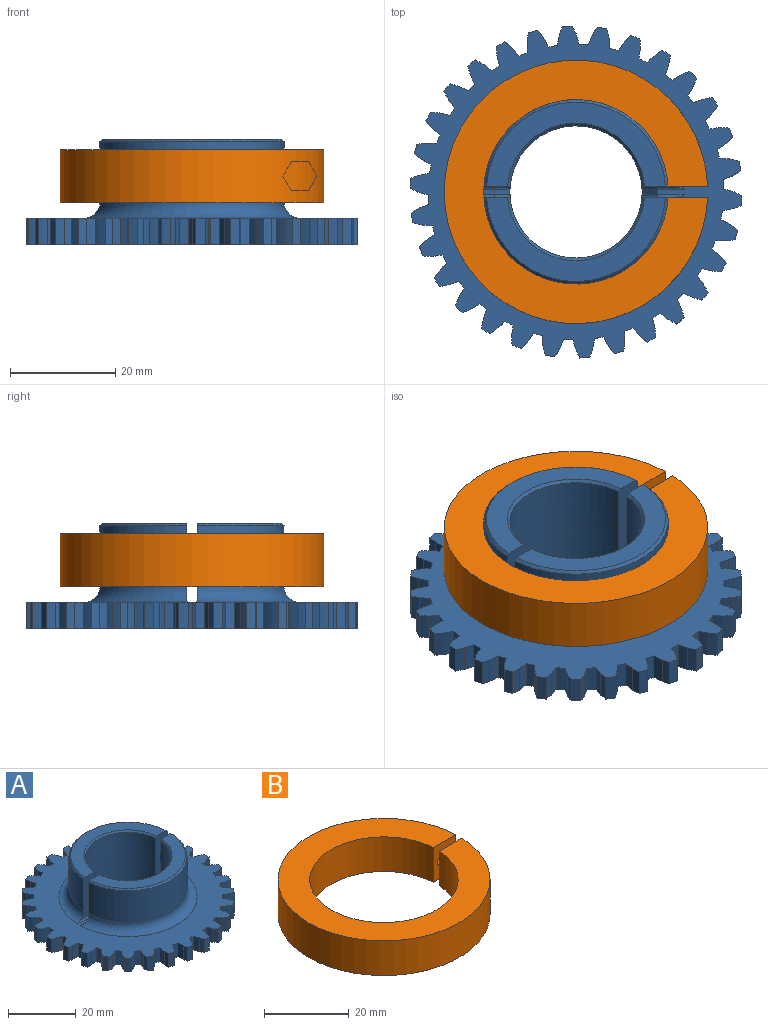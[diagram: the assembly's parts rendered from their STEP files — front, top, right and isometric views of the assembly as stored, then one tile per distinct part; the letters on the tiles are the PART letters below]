
ASSEMBLY  parts=2 mates=1
PART A: 208 faces, bbox 67.7x63x24 mm
  f0: cylinder r=12.55mm len=25.1mm, axis (0,0,-1), area 1428.8mm2, adj f4,f190,f191,f192,f193,f194,f195,f198
  f1: cylinder r=17.5mm len=34.94mm, axis (0,0,-1), area 609.2mm2, adj f3,f192,f194,f197
  f2: plane 33.94x16mm, normal (0,0,1), area 178.5mm2, adj f3,f4,f192,f194
  f3: cone r=17mm half-angle=45deg, axis (0,0,-1), area 36.9mm2, adj f1,f2,f192,f194
  f4: cone r=12.55mm half-angle=45deg, axis (0,0,1), area 27mm2, adj f0,f2,f192,f194
  f5: cylinder r=28mm len=5mm, axis (0,0,-1), area 8.7mm2, adj f9,f16,f181,f188
  f6: cylinder r=15.65mm len=5mm, axis (0,0,-1), area 8.3mm2, adj f7,f10,f181,f188
  f7: cylinder r=31.5mm len=5mm, axis (0,0,-1), area 9.1mm2, adj f6,f8,f181,f188
  f8: cylinder r=15.65mm len=5mm, axis (0,0,-1), area 8.3mm2, adj f7,f9,f181,f188
  f9: cylinder r=17.87mm len=5mm, axis (0,0,-1), area 10.5mm2, adj f5,f8,f181,f188
  f10: cylinder r=17.87mm len=5mm, axis (0,0,-1), area 10.5mm2, adj f6,f181,f182,f188
  f11: cylinder r=28mm len=5mm, axis (0,0,-1), area 8.7mm2, adj f15,f22,f181,f188
  f12: cylinder r=15.65mm len=5mm, axis (0,0,-1), area 8.3mm2, adj f13,f16,f181,f188
  f13: cylinder r=31.5mm len=5mm, axis (0,0,-1), area 9.1mm2, adj f12,f14,f181,f188
  f14: cylinder r=15.65mm len=5mm, axis (0,0,-1), area 8.3mm2, adj f13,f15,f181,f188
  f15: cylinder r=17.87mm len=5mm, axis (0,0,-1), area 10.5mm2, adj f11,f14,f181,f188
  f16: cylinder r=17.87mm len=5mm, axis (0,0,-1), area 10.5mm2, adj f5,f12,f181,f188
  f17: cylinder r=28mm len=5mm, axis (0,0,-1), area 8.7mm2, adj f21,f28,f181,f188
  f18: cylinder r=15.65mm len=5mm, axis (0,0,-1), area 8.3mm2, adj f19,f22,f181,f188
  f19: cylinder r=31.5mm len=5mm, axis (0,0,-1), area 9.1mm2, adj f18,f20,f181,f188
  f20: cylinder r=15.65mm len=5mm, axis (0,0,-1), area 8.3mm2, adj f19,f21,f181,f188
  f21: cylinder r=17.87mm len=5mm, axis (0,0,-1), area 10.5mm2, adj f17,f20,f181,f188
  f22: cylinder r=17.87mm len=5mm, axis (0,0,-1), area 10.5mm2, adj f11,f18,f181,f188
  f23: cylinder r=28mm len=5mm, axis (0,0,-1), area 8.7mm2, adj f27,f34,f181,f188
  f24: cylinder r=15.65mm len=5mm, axis (0,0,-1), area 8.3mm2, adj f25,f28,f181,f188
  f25: cylinder r=31.5mm len=5mm, axis (0,0,-1), area 9.1mm2, adj f24,f26,f181,f188
  f26: cylinder r=15.65mm len=5mm, axis (0,0,-1), area 8.3mm2, adj f25,f27,f181,f188
  f27: cylinder r=17.87mm len=5mm, axis (0,0,-1), area 10.5mm2, adj f23,f26,f181,f188
  f28: cylinder r=17.87mm len=5mm, axis (0,0,-1), area 10.5mm2, adj f17,f24,f181,f188
  f29: cylinder r=28mm len=5mm, axis (0,0,-1), area 8.7mm2, adj f33,f40,f181,f188
  f30: cylinder r=15.65mm len=5mm, axis (0,0,-1), area 8.3mm2, adj f31,f34,f181,f188
  f31: cylinder r=31.5mm len=5mm, axis (0,0,-1), area 9.1mm2, adj f30,f32,f181,f188
  f32: cylinder r=15.65mm len=5mm, axis (0,0,-1), area 8.3mm2, adj f31,f33,f181,f188
  f33: cylinder r=17.87mm len=5mm, axis (0,0,-1), area 10.5mm2, adj f29,f32,f181,f188
  f34: cylinder r=17.87mm len=5mm, axis (0,0,-1), area 10.5mm2, adj f23,f30,f181,f188
  f35: cylinder r=28mm len=5mm, axis (0,0,-1), area 8.7mm2, adj f39,f46,f181,f188
  f36: cylinder r=15.65mm len=5mm, axis (0,0,-1), area 8.3mm2, adj f37,f40,f181,f188
  f37: cylinder r=31.5mm len=5mm, axis (0,0,-1), area 9.1mm2, adj f36,f38,f181,f188
  f38: cylinder r=15.65mm len=5mm, axis (0,0,-1), area 8.3mm2, adj f37,f39,f181,f188
  f39: cylinder r=17.87mm len=5mm, axis (0,0,-1), area 10.5mm2, adj f35,f38,f181,f188
  f40: cylinder r=17.87mm len=5mm, axis (0,0,-1), area 10.5mm2, adj f29,f36,f181,f188
  f41: cylinder r=28mm len=5mm, axis (0,0,-1), area 8.7mm2, adj f45,f52,f181,f188
  f42: cylinder r=15.65mm len=5mm, axis (0,0,-1), area 8.3mm2, adj f43,f46,f181,f188
  f43: cylinder r=31.5mm len=5mm, axis (0,0,-1), area 9.1mm2, adj f42,f44,f181,f188
  f44: cylinder r=15.65mm len=5mm, axis (0,0,-1), area 8.3mm2, adj f43,f45,f181,f188
  f45: cylinder r=17.87mm len=5mm, axis (0,0,-1), area 10.5mm2, adj f41,f44,f181,f188
  f46: cylinder r=17.87mm len=5mm, axis (0,0,-1), area 10.5mm2, adj f35,f42,f181,f188
  f47: cylinder r=28mm len=5mm, axis (0,0,-1), area 8.7mm2, adj f51,f58,f181,f188
  f48: cylinder r=15.65mm len=5mm, axis (0,0,-1), area 8.3mm2, adj f49,f52,f181,f188
  f49: cylinder r=31.5mm len=5mm, axis (0,0,-1), area 9.1mm2, adj f48,f50,f181,f188
  f50: cylinder r=15.65mm len=5mm, axis (0,0,-1), area 8.3mm2, adj f49,f51,f181,f188
  f51: cylinder r=17.87mm len=5mm, axis (0,0,-1), area 10.5mm2, adj f47,f50,f181,f188
  f52: cylinder r=17.87mm len=5mm, axis (0,0,-1), area 10.5mm2, adj f41,f48,f181,f188
  f53: cylinder r=28mm len=5mm, axis (0,0,-1), area 8.7mm2, adj f57,f64,f181,f188
  f54: cylinder r=15.65mm len=5mm, axis (0,0,-1), area 8.3mm2, adj f55,f58,f181,f188
  f55: cylinder r=31.5mm len=5mm, axis (0,0,-1), area 9.1mm2, adj f54,f56,f181,f188
  f56: cylinder r=15.65mm len=5mm, axis (0,0,-1), area 8.3mm2, adj f55,f57,f181,f188
  f57: cylinder r=17.87mm len=5mm, axis (0,0,-1), area 10.5mm2, adj f53,f56,f181,f188
  f58: cylinder r=17.87mm len=5mm, axis (0,0,-1), area 10.5mm2, adj f47,f54,f181,f188
  f59: cylinder r=28mm len=5mm, axis (0,0,-1), area 8.7mm2, adj f63,f70,f181,f188
  f60: cylinder r=15.65mm len=5mm, axis (0,0,-1), area 8.3mm2, adj f61,f64,f181,f188
  f61: cylinder r=31.5mm len=5mm, axis (0,0,-1), area 9.1mm2, adj f60,f62,f181,f188
  f62: cylinder r=15.65mm len=5mm, axis (0,0,-1), area 8.3mm2, adj f61,f63,f181,f188
  f63: cylinder r=17.87mm len=5mm, axis (0,0,-1), area 10.5mm2, adj f59,f62,f181,f188
  f64: cylinder r=17.87mm len=5mm, axis (0,0,-1), area 10.5mm2, adj f53,f60,f181,f188
  f65: cylinder r=28mm len=5mm, axis (0,0,-1), area 8.7mm2, adj f69,f76,f181,f188
  f66: cylinder r=15.65mm len=5mm, axis (0,0,-1), area 8.3mm2, adj f67,f70,f181,f188
  f67: cylinder r=31.5mm len=5mm, axis (0,0,-1), area 9.1mm2, adj f66,f68,f181,f188
  f68: cylinder r=15.65mm len=5mm, axis (0,0,-1), area 8.3mm2, adj f67,f69,f181,f188
  f69: cylinder r=17.87mm len=5mm, axis (0,0,-1), area 10.5mm2, adj f65,f68,f181,f188
  f70: cylinder r=17.87mm len=5mm, axis (0,0,-1), area 10.5mm2, adj f59,f66,f181,f188
  f71: cylinder r=28mm len=5mm, axis (0,0,-1), area 8.7mm2, adj f75,f82,f181,f188
  f72: cylinder r=15.65mm len=5mm, axis (0,0,-1), area 8.3mm2, adj f73,f76,f181,f188
  f73: cylinder r=31.5mm len=5mm, axis (0,0,-1), area 9.1mm2, adj f72,f74,f181,f188
  f74: cylinder r=15.65mm len=5mm, axis (0,0,-1), area 8.3mm2, adj f73,f75,f181,f188
  f75: cylinder r=17.87mm len=5mm, axis (0,0,-1), area 10.5mm2, adj f71,f74,f181,f188
  f76: cylinder r=17.87mm len=5mm, axis (0,0,-1), area 10.5mm2, adj f65,f72,f181,f188
  f77: cylinder r=28mm len=5mm, axis (0,0,-1), area 8.7mm2, adj f81,f88,f181,f188
  f78: cylinder r=15.65mm len=5mm, axis (0,0,-1), area 8.3mm2, adj f79,f82,f181,f188
  f79: cylinder r=31.5mm len=5mm, axis (0,0,-1), area 9.1mm2, adj f78,f80,f181,f188
  f80: cylinder r=15.65mm len=5mm, axis (0,0,-1), area 8.3mm2, adj f79,f81,f181,f188
  f81: cylinder r=17.87mm len=5mm, axis (0,0,-1), area 10.5mm2, adj f77,f80,f181,f188
  f82: cylinder r=17.87mm len=5mm, axis (0,0,-1), area 10.5mm2, adj f71,f78,f181,f188
  f83: cylinder r=28mm len=5mm, axis (0,0,-1), area 8.7mm2, adj f87,f94,f181,f188
  f84: cylinder r=15.65mm len=5mm, axis (0,0,-1), area 8.3mm2, adj f85,f88,f181,f188
  f85: cylinder r=31.5mm len=5mm, axis (0,0,-1), area 9.1mm2, adj f84,f86,f181,f188
  f86: cylinder r=15.65mm len=5mm, axis (0,0,-1), area 8.3mm2, adj f85,f87,f181,f188
  f87: cylinder r=17.87mm len=5mm, axis (0,0,-1), area 10.5mm2, adj f83,f86,f181,f188
  f88: cylinder r=17.87mm len=5mm, axis (0,0,-1), area 10.5mm2, adj f77,f84,f181,f188
  f89: cylinder r=28mm len=5mm, axis (0,0,-1), area 8.7mm2, adj f93,f100,f181,f188
  f90: cylinder r=15.65mm len=5mm, axis (0,0,-1), area 8.3mm2, adj f91,f94,f181,f188
  f91: cylinder r=31.5mm len=5mm, axis (0,0,-1), area 9.1mm2, adj f90,f92,f181,f188
  f92: cylinder r=15.65mm len=5mm, axis (0,0,-1), area 8.3mm2, adj f91,f93,f181,f188
  f93: cylinder r=17.87mm len=5mm, axis (0,0,-1), area 10.5mm2, adj f89,f92,f181,f188
  f94: cylinder r=17.87mm len=5mm, axis (0,0,-1), area 10.5mm2, adj f83,f90,f181,f188
  f95: cylinder r=28mm len=5mm, axis (0,0,-1), area 8.7mm2, adj f99,f106,f181,f188
  f96: cylinder r=15.65mm len=5mm, axis (0,0,-1), area 8.3mm2, adj f97,f100,f181,f188
  f97: cylinder r=31.5mm len=5mm, axis (0,0,-1), area 9.1mm2, adj f96,f98,f181,f188
  f98: cylinder r=15.65mm len=5mm, axis (0,0,-1), area 8.3mm2, adj f97,f99,f181,f188
  f99: cylinder r=17.87mm len=5mm, axis (0,0,-1), area 10.5mm2, adj f95,f98,f181,f188
  f100: cylinder r=17.87mm len=5mm, axis (0,0,-1), area 10.5mm2, adj f89,f96,f181,f188
  f101: cylinder r=28mm len=5mm, axis (0,0,-1), area 8.7mm2, adj f105,f112,f181,f188
  f102: cylinder r=15.65mm len=5mm, axis (0,0,-1), area 8.3mm2, adj f103,f106,f181,f188
  f103: cylinder r=31.5mm len=5mm, axis (0,0,-1), area 9.1mm2, adj f102,f104,f181,f188
  f104: cylinder r=15.65mm len=5mm, axis (0,0,-1), area 8.3mm2, adj f103,f105,f181,f188
  f105: cylinder r=17.87mm len=5mm, axis (0,0,-1), area 10.5mm2, adj f101,f104,f181,f188
  f106: cylinder r=17.87mm len=5mm, axis (0,0,-1), area 10.5mm2, adj f95,f102,f181,f188
  f107: cylinder r=28mm len=5mm, axis (0,0,-1), area 8.7mm2, adj f111,f118,f181,f188
  f108: cylinder r=15.65mm len=5mm, axis (0,0,-1), area 8.3mm2, adj f109,f112,f181,f188
  f109: cylinder r=31.5mm len=5mm, axis (0,0,-1), area 9.1mm2, adj f108,f110,f181,f188
  f110: cylinder r=15.65mm len=5mm, axis (0,0,-1), area 8.3mm2, adj f109,f111,f181,f188
  f111: cylinder r=17.87mm len=5mm, axis (0,0,-1), area 10.5mm2, adj f107,f110,f181,f188
  f112: cylinder r=17.87mm len=5mm, axis (0,0,-1), area 10.5mm2, adj f101,f108,f181,f188
  f113: cylinder r=28mm len=5mm, axis (0,0,-1), area 8.7mm2, adj f117,f124,f181,f188
  f114: cylinder r=15.65mm len=5mm, axis (0,0,-1), area 8.3mm2, adj f115,f118,f181,f188
  f115: cylinder r=31.5mm len=5mm, axis (0,0,-1), area 9.1mm2, adj f114,f116,f181,f188
  f116: cylinder r=15.65mm len=5mm, axis (0,0,-1), area 8.3mm2, adj f115,f117,f181,f188
  f117: cylinder r=17.87mm len=5mm, axis (0,0,-1), area 10.5mm2, adj f113,f116,f181,f188
  f118: cylinder r=17.87mm len=5mm, axis (0,0,-1), area 10.5mm2, adj f107,f114,f181,f188
  f119: cylinder r=28mm len=5mm, axis (0,0,-1), area 8.7mm2, adj f123,f130,f181,f188
  f120: cylinder r=15.65mm len=5mm, axis (0,0,-1), area 8.3mm2, adj f121,f124,f181,f188
  f121: cylinder r=31.5mm len=5mm, axis (0,0,-1), area 9.1mm2, adj f120,f122,f181,f188
  f122: cylinder r=15.65mm len=5mm, axis (0,0,-1), area 8.3mm2, adj f121,f123,f181,f188
  f123: cylinder r=17.87mm len=5mm, axis (0,0,-1), area 10.5mm2, adj f119,f122,f181,f188
  f124: cylinder r=17.87mm len=5mm, axis (0,0,-1), area 10.5mm2, adj f113,f120,f181,f188
  f125: cylinder r=28mm len=5mm, axis (0,0,-1), area 8.7mm2, adj f129,f136,f181,f188
  f126: cylinder r=15.65mm len=5mm, axis (0,0,-1), area 8.3mm2, adj f127,f130,f181,f188
  f127: cylinder r=31.5mm len=5mm, axis (0,0,-1), area 9.1mm2, adj f126,f128,f181,f188
  f128: cylinder r=15.65mm len=5mm, axis (0,0,-1), area 8.3mm2, adj f127,f129,f181,f188
  f129: cylinder r=17.87mm len=5mm, axis (0,0,-1), area 10.5mm2, adj f125,f128,f181,f188
  f130: cylinder r=17.87mm len=5mm, axis (0,0,-1), area 10.5mm2, adj f119,f126,f181,f188
  f131: cylinder r=28mm len=5mm, axis (0,0,-1), area 8.7mm2, adj f135,f142,f181,f188
  f132: cylinder r=15.65mm len=5mm, axis (0,0,-1), area 8.3mm2, adj f133,f136,f181,f188
  f133: cylinder r=31.5mm len=5mm, axis (0,0,-1), area 9.1mm2, adj f132,f134,f181,f188
  f134: cylinder r=15.65mm len=5mm, axis (0,0,-1), area 8.3mm2, adj f133,f135,f181,f188
  f135: cylinder r=17.87mm len=5mm, axis (0,0,-1), area 10.5mm2, adj f131,f134,f181,f188
  f136: cylinder r=17.87mm len=5mm, axis (0,0,-1), area 10.5mm2, adj f125,f132,f181,f188
  f137: cylinder r=28mm len=5mm, axis (0,0,-1), area 8.7mm2, adj f141,f148,f181,f188
  f138: cylinder r=15.65mm len=5mm, axis (0,0,-1), area 8.3mm2, adj f139,f142,f181,f188
  f139: cylinder r=31.5mm len=5mm, axis (0,0,-1), area 9.1mm2, adj f138,f140,f181,f188
  f140: cylinder r=15.65mm len=5mm, axis (0,0,-1), area 8.3mm2, adj f139,f141,f181,f188
  f141: cylinder r=17.87mm len=5mm, axis (0,0,-1), area 10.5mm2, adj f137,f140,f181,f188
  f142: cylinder r=17.87mm len=5mm, axis (0,0,-1), area 10.5mm2, adj f131,f138,f181,f188
  f143: cylinder r=28mm len=5mm, axis (0,0,-1), area 8.7mm2, adj f147,f154,f181,f188
  f144: cylinder r=15.65mm len=5mm, axis (0,0,-1), area 8.3mm2, adj f145,f148,f181,f188
  f145: cylinder r=31.5mm len=5mm, axis (0,0,-1), area 9.1mm2, adj f144,f146,f181,f188
  f146: cylinder r=15.65mm len=5mm, axis (0,0,-1), area 8.3mm2, adj f145,f147,f181,f188
  f147: cylinder r=17.87mm len=5mm, axis (0,0,-1), area 10.5mm2, adj f143,f146,f181,f188
  f148: cylinder r=17.87mm len=5mm, axis (0,0,-1), area 10.5mm2, adj f137,f144,f181,f188
  f149: cylinder r=28mm len=5mm, axis (0,0,-1), area 8.7mm2, adj f153,f160,f181,f188
  f150: cylinder r=15.65mm len=5mm, axis (0,0,-1), area 8.3mm2, adj f151,f154,f181,f188
  f151: cylinder r=31.5mm len=5mm, axis (0,0,-1), area 9.1mm2, adj f150,f152,f181,f188
  f152: cylinder r=15.65mm len=5mm, axis (0,0,-1), area 8.3mm2, adj f151,f153,f181,f188
  f153: cylinder r=17.87mm len=5mm, axis (0,0,-1), area 10.5mm2, adj f149,f152,f181,f188
  f154: cylinder r=17.87mm len=5mm, axis (0,0,-1), area 10.5mm2, adj f143,f150,f181,f188
  f155: cylinder r=28mm len=5mm, axis (0,0,-1), area 8.7mm2, adj f159,f166,f181,f188
  f156: cylinder r=15.65mm len=5mm, axis (0,0,-1), area 8.3mm2, adj f157,f160,f181,f188
  f157: cylinder r=31.5mm len=5mm, axis (0,0,-1), area 9.1mm2, adj f156,f158,f181,f188
  f158: cylinder r=15.65mm len=5mm, axis (0,0,-1), area 8.3mm2, adj f157,f159,f181,f188
  f159: cylinder r=17.87mm len=5mm, axis (0,0,-1), area 10.5mm2, adj f155,f158,f181,f188
  f160: cylinder r=17.87mm len=5mm, axis (0,0,-1), area 10.5mm2, adj f149,f156,f181,f188
  f161: cylinder r=28mm len=5mm, axis (0,0,-1), area 8.7mm2, adj f165,f172,f181,f188
  f162: cylinder r=15.65mm len=5mm, axis (0,0,-1), area 8.3mm2, adj f163,f166,f181,f188
  f163: cylinder r=31.5mm len=5mm, axis (0,0,-1), area 9.1mm2, adj f162,f164,f181,f188
  f164: cylinder r=15.65mm len=5mm, axis (0,0,-1), area 8.3mm2, adj f163,f165,f181,f188
  f165: cylinder r=17.87mm len=5mm, axis (0,0,-1), area 10.5mm2, adj f161,f164,f181,f188
  f166: cylinder r=17.87mm len=5mm, axis (0,0,-1), area 10.5mm2, adj f155,f162,f181,f188
  f167: cylinder r=28mm len=5mm, axis (0,0,-1), area 8.7mm2, adj f171,f178,f181,f188
  f168: cylinder r=15.65mm len=5mm, axis (0,0,-1), area 8.3mm2, adj f169,f172,f181,f188
  f169: cylinder r=31.5mm len=5mm, axis (0,0,-1), area 9.1mm2, adj f168,f170,f181,f188
  f170: cylinder r=15.65mm len=5mm, axis (0,0,-1), area 8.3mm2, adj f169,f171,f181,f188
  f171: cylinder r=17.87mm len=5mm, axis (0,0,-1), area 10.5mm2, adj f167,f170,f181,f188
  f172: cylinder r=17.87mm len=5mm, axis (0,0,-1), area 10.5mm2, adj f161,f168,f181,f188
  f173: cylinder r=28mm len=5mm, axis (0,0,-1), area 8.7mm2, adj f177,f181,f183,f188
  f174: cylinder r=15.65mm len=5mm, axis (0,0,-1), area 8.3mm2, adj f175,f178,f181,f188
  f175: cylinder r=31.5mm len=5mm, axis (0,0,-1), area 9.1mm2, adj f174,f176,f181,f188
  f176: cylinder r=15.65mm len=5mm, axis (0,0,-1), area 8.3mm2, adj f175,f177,f181,f188
  f177: cylinder r=17.87mm len=5mm, axis (0,0,-1), area 10.5mm2, adj f173,f176,f181,f188
  f178: cylinder r=17.87mm len=5mm, axis (0,0,-1), area 10.5mm2, adj f167,f174,f181,f188
  f179: cylinder r=17.5mm len=34.94mm, axis (0,0,-1), area 609.2mm2, adj f189,f193,f195,f196
  f180: plane 33.94x16mm, normal (0,0,1), area 178.5mm2, adj f189,f191,f193,f195
  f181: plane 62.98x62.98mm, normal (0,0,-1), area 2262mm2, adj f5,f6,f7,f8,f9,f10,f11,f12
  f182: cylinder r=28mm len=5mm, axis (0,0,-1), area 8.7mm2, adj f10,f181,f187,f188
  f183: cylinder r=17.87mm len=5mm, axis (0,0,-1), area 10.5mm2, adj f173,f181,f184,f188
  f184: cylinder r=15.65mm len=5mm, axis (0,0,-1), area 8.3mm2, adj f181,f183,f185,f188
  f185: cylinder r=31.5mm len=5mm, axis (0,0,-1), area 9.1mm2, adj f181,f184,f186,f188
  f186: cylinder r=15.65mm len=5mm, axis (0,0,-1), area 8.3mm2, adj f181,f185,f187,f188
  f187: cylinder r=17.87mm len=5mm, axis (0,0,-1), area 10.5mm2, adj f181,f182,f186,f188
  f188: plane 62.98x62.98mm, normal (0,0,1), area 1486.6mm2, adj f5,f6,f7,f8,f9,f10,f11,f12
  f189: cone r=17mm half-angle=45deg, axis (0,0,-1), area 36.9mm2, adj f179,f180,f193,f195
  f190: cone r=13.05mm half-angle=45deg, axis (0,0,-1), area 56.9mm2, adj f0,f181
  f191: cone r=12.55mm half-angle=45deg, axis (0,0,1), area 27mm2, adj f0,f180,f193,f195
  f192: plane 17.35x6.34mm, normal (0,-1,0), area 76.7mm2, adj f0,f1,f2,f3,f4,f197,f206,f207
  f193: plane 17.35x6.34mm, normal (0,1,0), area 76.7mm2, adj f0,f179,f180,f189,f191,f196,f204,f205
  f194: plane 17.35x6.34mm, normal (0,-1,0), area 76.7mm2, adj f0,f1,f2,f3,f4,f197,f200,f201
  f195: plane 17.35x6.34mm, normal (0,1,0), area 76.7mm2, adj f0,f179,f180,f189,f191,f196,f202,f203
  f196: torus R=20.5mm, axis (0,0,1), area 266.7mm2, adj f179,f188,f193,f195,f202,f204
  f197: torus R=20.5mm, axis (0,0,1), area 266.7mm2, adj f1,f188,f192,f194,f200,f206
  f198: cone r=12.55mm half-angle=45deg, axis (0,0,1), area 4.4mm2, adj f0,f188,f204,f205,f206,f207
  f199: cone r=12.55mm half-angle=45deg, axis (0,0,1), area 4.4mm2, adj f0,f188,f200,f201,f202,f203
  f200: cylinder r=0.5mm len=5.16mm, axis (-1,0,0), area 3.2mm2, adj f188,f194,f197,f199,f201
  f201: bspline ~23.95x23.94mm, area 3.2mm2, adj f0,f194,f199,f200
  f202: cylinder r=0.5mm len=5.16mm, axis (1,0,0), area 3.2mm2, adj f188,f195,f196,f199,f203
  f203: bspline ~23.95x23.94mm, area 3.2mm2, adj f0,f195,f199,f202
  f204: cylinder r=0.5mm len=5.16mm, axis (1,0,0), area 3.2mm2, adj f188,f193,f196,f198,f205
  f205: bspline ~23.95x23.94mm, area 3.2mm2, adj f0,f193,f198,f204
  f206: cylinder r=0.5mm len=5.16mm, axis (-1,0,0), area 3.2mm2, adj f188,f192,f197,f198,f207
  f207: bspline ~23.95x23.94mm, area 3.2mm2, adj f0,f192,f198,f206
PART B: 19 faces, bbox 50x50.1x10.1 mm
  f0: cylinder r=25mm len=50mm, axis (0,0,-1), area 1499.6mm2, adj f1,f2,f3,f4,f5
  f1: plane 10x7.51mm, normal (0,-1,0), area 67mm2, adj f0,f2,f4,f6,f7
  f2: plane 50x49.98mm, normal (0,0,-1), area 986.4mm2, adj f0,f1,f3,f7
  f3: plane 10x7.51mm, normal (0,1,0), area 67mm2, adj f0,f2,f4,f7,f8
  f4: plane 50x49.98mm, normal (0,0,1), area 986.4mm2, adj f0,f1,f3,f7
  f5: cylinder r=3mm len=12.88mm, axis (0,-1,0), area 166.3mm2, adj f0,f9
  f6: cylinder r=1.6mm len=3.2mm, axis (0,-1,0), area 30.2mm2, adj f1,f10
  f7: cylinder r=17.5mm len=35mm, axis (0,0,-1), area 1079.5mm2, adj f1,f2,f3,f4
  f8: cylinder r=1.6mm len=4mm, axis (0,-1,0), area 40.2mm2, adj f3,f11
  f9: plane 6x6mm, normal (0,1,0), area 7mm2, adj f5,f10
  f10: cone r=1.6mm half-angle=45deg, axis (0,1,0), area 18.7mm2, adj f6,f9
  f11: plane 6.47x5.6mm, normal (0,-1,0), area 19.1mm2, adj f8,f12,f13,f14,f15,f16,f17
  f12: plane 11.42x3.23mm, normal (0,0,1), area 29.9mm2, adj f11,f13,f17,f18
  f13: plane 6.71x2.8mm, normal (-0.87,0,0.5), area 16.1mm2, adj f11,f12,f14,f18
  f14: plane 6.71x2.8mm, normal (-0.87,0,-0.5), area 16.1mm2, adj f11,f13,f15,f18
  f15: plane 11.42x3.23mm, normal (0,0,-1), area 29.9mm2, adj f11,f14,f16,f18
  f16: plane 13.17x2.87mm, normal (0.87,0,-0.5), area 39.7mm2, adj f11,f15,f17,f18
  f17: plane 13.17x2.87mm, normal (0.87,0,0.5), area 39.7mm2, adj f11,f12,f16,f18
  f18: cylinder r=25mm len=10.16mm, axis (0,0,-1), area 49.4mm2, adj f12,f13,f14,f15,f16,f17
PLACE A t=(5.86,2.63,-11.12)mm
PLACE B t=(5.86,2.63,-3.12)mm
MATE fastened B.f7 <-> A.f1  axis (0,0,-1) through (5.86,2.63,-3.12)mm
